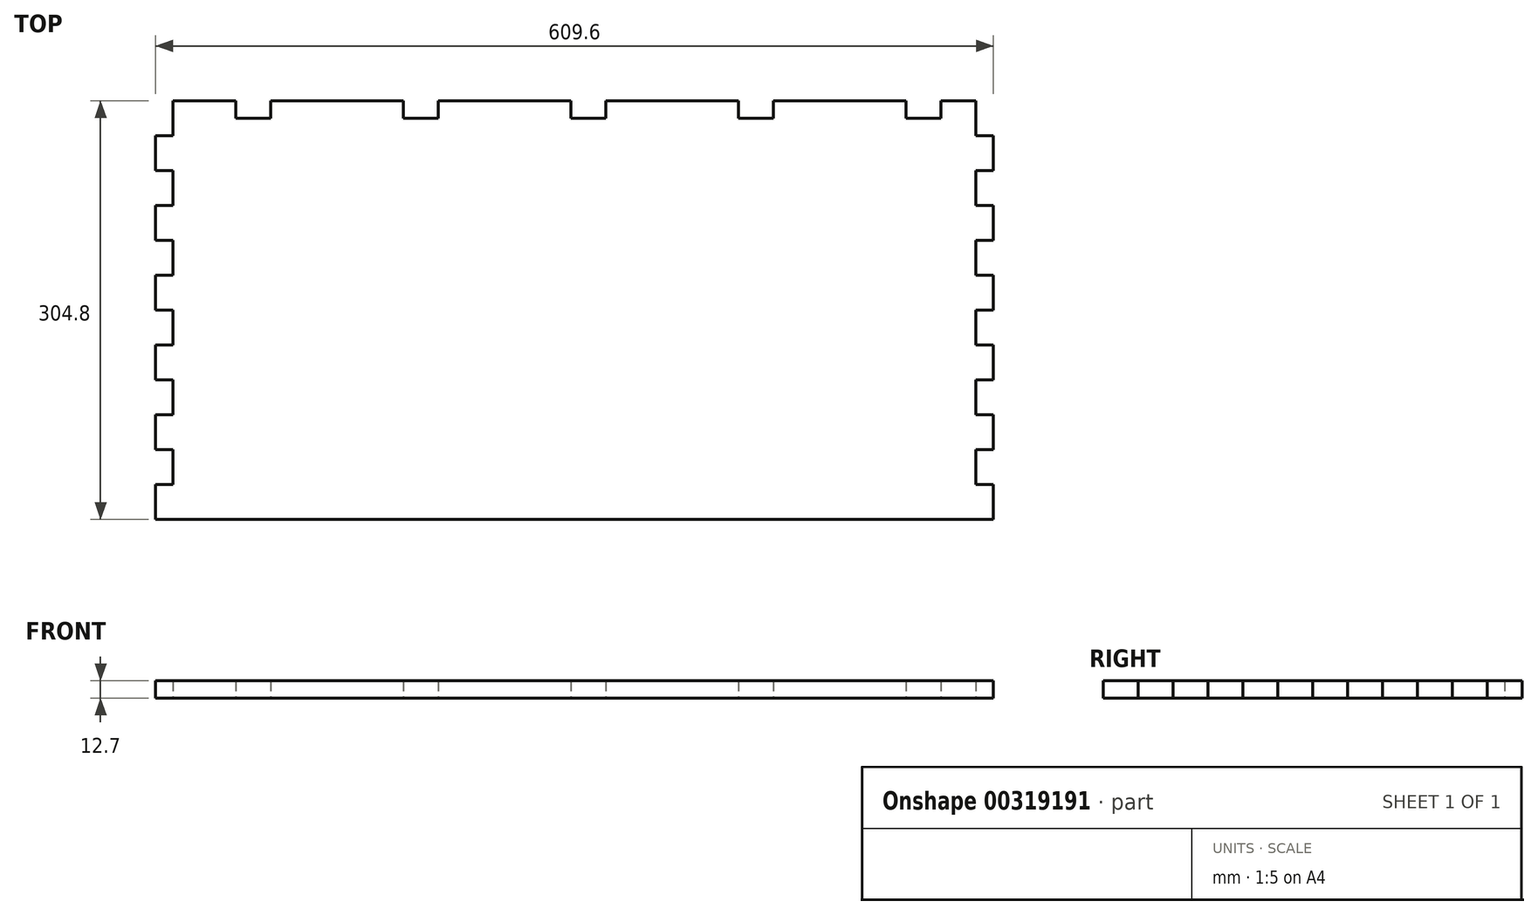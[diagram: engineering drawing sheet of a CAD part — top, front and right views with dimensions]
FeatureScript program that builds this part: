
annotation { "Feature Type Name" : "Feature", "Feature Type Description" : "" }
export const myFeature = defineFeature(function(context is Context, id is Id, definition is map)
    precondition{}
    {
        {
            var Q0;
            Q0=qCreatedBy(makeId("Top.planeOp"),FACE);
            var sketch = newSketch(context, id + "F0", { "sketchPlane" : qUnion([Q0])});
            skLineSegment(sketch, "E0.bottom", {"start": v(-304.8, 152.4) * mm, "end": v(304.8, 152.4) * mm});
            skLineSegment(sketch, "E0.top", {"start": v(-304.8, -152.4) * mm, "end": v(304.8, -152.4) * mm});
            skLineSegment(sketch, "E0.left", {"start": v(-304.8, 152.4) * mm, "end": v(-304.8, -152.4) * mm});
            skLineSegment(sketch, "E0.right", {"start": v(304.8, 152.4) * mm, "end": v(304.8, -152.4) * mm});
            skPoint(sketch, "E0.middle", {"position": v(0, 0) * mm});
            skLineSegment(sketch, "E1.bottom", {"start": v(-304.8, 152.4) * mm, "end": v(-292.1, 152.4) * mm});
            skLineSegment(sketch, "E1.top", {"start": v(-304.8, 127) * mm, "end": v(-292.1, 127) * mm});
            skLineSegment(sketch, "E1.left", {"start": v(-304.8, 152.4) * mm, "end": v(-304.8, 127) * mm});
            skLineSegment(sketch, "E1.right", {"start": v(-292.1, 152.4) * mm, "end": v(-292.1, 127) * mm});
            skLineSegment(sketch, "E2.0.1.0", {"start": v(-304.8, 76.2) * mm, "end": v(-292.1, 76.2) * mm});
            skLineSegment(sketch, "E2.0.1.1", {"start": v(-304.8, 101.6) * mm, "end": v(-292.1, 101.6) * mm});
            skLineSegment(sketch, "E2.0.1.2", {"start": v(-292.1, 101.6) * mm, "end": v(-292.1, 76.2) * mm});
            skLineSegment(sketch, "E2.0.1.3", {"start": v(-304.8, 101.6) * mm, "end": v(-304.8, 76.2) * mm});
            skLineSegment(sketch, "E2.0.2.0", {"start": v(-304.8, 25.4) * mm, "end": v(-292.1, 25.4) * mm});
            skLineSegment(sketch, "E2.0.2.1", {"start": v(-304.8, 50.8) * mm, "end": v(-292.1, 50.8) * mm});
            skLineSegment(sketch, "E2.0.2.2", {"start": v(-292.1, 50.8) * mm, "end": v(-292.1, 25.4) * mm});
            skLineSegment(sketch, "E2.0.2.3", {"start": v(-304.8, 50.8) * mm, "end": v(-304.8, 25.4) * mm});
            skLineSegment(sketch, "E2.0.3.0", {"start": v(-304.8, -25.4) * mm, "end": v(-292.1, -25.4) * mm});
            skLineSegment(sketch, "E2.0.3.1", {"start": v(-304.8, 0) * mm, "end": v(-292.1, 0) * mm});
            skLineSegment(sketch, "E2.0.3.2", {"start": v(-292.1, 0) * mm, "end": v(-292.1, -25.4) * mm});
            skLineSegment(sketch, "E2.0.3.3", {"start": v(-304.8, 0) * mm, "end": v(-304.8, -25.4) * mm});
            skLineSegment(sketch, "E2.0.4.0", {"start": v(-304.8, -76.2) * mm, "end": v(-292.1, -76.2) * mm});
            skLineSegment(sketch, "E2.0.4.1", {"start": v(-304.8, -50.8) * mm, "end": v(-292.1, -50.8) * mm});
            skLineSegment(sketch, "E2.0.4.2", {"start": v(-292.1, -50.8) * mm, "end": v(-292.1, -76.2) * mm});
            skLineSegment(sketch, "E2.0.4.3", {"start": v(-304.8, -50.8) * mm, "end": v(-304.8, -76.2) * mm});
            skLineSegment(sketch, "E2.0.5.0", {"start": v(-304.8, -127) * mm, "end": v(-292.1, -127) * mm});
            skLineSegment(sketch, "E2.0.5.1", {"start": v(-304.8, -101.6) * mm, "end": v(-292.1, -101.6) * mm});
            skLineSegment(sketch, "E2.0.5.2", {"start": v(-292.1, -101.6) * mm, "end": v(-292.1, -127) * mm});
            skLineSegment(sketch, "E2.0.5.3", {"start": v(-304.8, -101.6) * mm, "end": v(-304.8, -127) * mm});
            skLineSegment(sketch, "E2.direction1", {"start": v(-304.8, 127) * mm, "end": v(-279.4, 127) * mm, "construction": true});
            skLineSegment(sketch, "E2.direction2", {"start": v(-304.8, 127) * mm, "end": v(-304.8, 76.2) * mm, "construction": true});
            skLineSegment(sketch, "E3.bottom", {"start": v(304.8, 152.4) * mm, "end": v(292.1, 152.4) * mm});
            skLineSegment(sketch, "E3.top", {"start": v(304.8, 127) * mm, "end": v(292.1, 127) * mm});
            skLineSegment(sketch, "E3.left", {"start": v(304.8, 152.4) * mm, "end": v(304.8, 127) * mm});
            skLineSegment(sketch, "E3.right", {"start": v(292.1, 152.4) * mm, "end": v(292.1, 127) * mm});
            skLineSegment(sketch, "E4.0.1.0", {"start": v(304.8, 76.2) * mm, "end": v(292.1, 76.2) * mm});
            skLineSegment(sketch, "E4.0.1.1", {"start": v(304.8, 101.6) * mm, "end": v(304.8, 76.2) * mm});
            skLineSegment(sketch, "E4.0.1.2", {"start": v(304.8, 101.6) * mm, "end": v(292.1, 101.6) * mm});
            skLineSegment(sketch, "E4.0.1.3", {"start": v(292.1, 101.6) * mm, "end": v(292.1, 76.2) * mm});
            skLineSegment(sketch, "E4.0.2.0", {"start": v(304.8, 25.4) * mm, "end": v(292.1, 25.4) * mm});
            skLineSegment(sketch, "E4.0.2.1", {"start": v(304.8, 50.8) * mm, "end": v(304.8, 25.4) * mm});
            skLineSegment(sketch, "E4.0.2.2", {"start": v(304.8, 50.8) * mm, "end": v(292.1, 50.8) * mm});
            skLineSegment(sketch, "E4.0.2.3", {"start": v(292.1, 50.8) * mm, "end": v(292.1, 25.4) * mm});
            skLineSegment(sketch, "E4.0.3.0", {"start": v(304.8, -25.4) * mm, "end": v(292.1, -25.4) * mm});
            skLineSegment(sketch, "E4.0.3.1", {"start": v(304.8, 0) * mm, "end": v(304.8, -25.4) * mm});
            skLineSegment(sketch, "E4.0.3.2", {"start": v(304.8, 0) * mm, "end": v(292.1, 0) * mm});
            skLineSegment(sketch, "E4.0.3.3", {"start": v(292.1, 0) * mm, "end": v(292.1, -25.4) * mm});
            skLineSegment(sketch, "E4.0.4.0", {"start": v(304.8, -76.2) * mm, "end": v(292.1, -76.2) * mm});
            skLineSegment(sketch, "E4.0.4.1", {"start": v(304.8, -50.8) * mm, "end": v(304.8, -76.2) * mm});
            skLineSegment(sketch, "E4.0.4.2", {"start": v(304.8, -50.8) * mm, "end": v(292.1, -50.8) * mm});
            skLineSegment(sketch, "E4.0.4.3", {"start": v(292.1, -50.8) * mm, "end": v(292.1, -76.2) * mm});
            skLineSegment(sketch, "E4.0.5.0", {"start": v(304.8, -127) * mm, "end": v(292.1, -127) * mm});
            skLineSegment(sketch, "E4.0.5.1", {"start": v(304.8, -101.6) * mm, "end": v(304.8, -127) * mm});
            skLineSegment(sketch, "E4.0.5.2", {"start": v(304.8, -101.6) * mm, "end": v(292.1, -101.6) * mm});
            skLineSegment(sketch, "E4.0.5.3", {"start": v(292.1, -101.6) * mm, "end": v(292.1, -127) * mm});
            skLineSegment(sketch, "E4.direction1", {"start": v(292.1, 127) * mm, "end": v(317.5, 127) * mm, "construction": true});
            skLineSegment(sketch, "E4.direction2", {"start": v(292.1, 127) * mm, "end": v(292.1, 76.2) * mm, "construction": true});
            skLineSegment(sketch, "E5.bottom", {"start": v(266.7, 152.4) * mm, "end": v(241.3, 152.4) * mm});
            skLineSegment(sketch, "E5.top", {"start": v(266.7, 139.7) * mm, "end": v(241.3, 139.7) * mm});
            skLineSegment(sketch, "E5.left", {"start": v(266.7, 152.4) * mm, "end": v(266.7, 139.7) * mm});
            skLineSegment(sketch, "E5.right", {"start": v(241.3, 152.4) * mm, "end": v(241.3, 139.7) * mm});
            skLineSegment(sketch, "E6.1.0.0", {"start": v(119.38, 152.4) * mm, "end": v(119.38, 139.7) * mm});
            skLineSegment(sketch, "E6.1.0.1", {"start": v(144.78, 139.7) * mm, "end": v(119.38, 139.7) * mm});
            skLineSegment(sketch, "E6.1.0.2", {"start": v(144.78, 152.4) * mm, "end": v(144.78, 139.7) * mm});
            skLineSegment(sketch, "E6.1.0.3", {"start": v(144.78, 152.4) * mm, "end": v(119.38, 152.4) * mm});
            skLineSegment(sketch, "E6.2.0.0", {"start": v(-2.54, 152.4) * mm, "end": v(-2.54, 139.7) * mm});
            skLineSegment(sketch, "E6.2.0.1", {"start": v(22.86, 139.7) * mm, "end": v(-2.54, 139.7) * mm});
            skLineSegment(sketch, "E6.2.0.2", {"start": v(22.86, 152.4) * mm, "end": v(22.86, 139.7) * mm});
            skLineSegment(sketch, "E6.2.0.3", {"start": v(22.86, 152.4) * mm, "end": v(-2.54, 152.4) * mm});
            skLineSegment(sketch, "E6.3.0.0", {"start": v(-124.46, 152.4) * mm, "end": v(-124.46, 139.7) * mm});
            skLineSegment(sketch, "E6.3.0.1", {"start": v(-99.06, 139.7) * mm, "end": v(-124.46, 139.7) * mm});
            skLineSegment(sketch, "E6.3.0.2", {"start": v(-99.06, 152.4) * mm, "end": v(-99.06, 139.7) * mm});
            skLineSegment(sketch, "E6.3.0.3", {"start": v(-99.06, 152.4) * mm, "end": v(-124.46, 152.4) * mm});
            skLineSegment(sketch, "E6.4.0.0", {"start": v(-246.38, 152.4) * mm, "end": v(-246.38, 139.7) * mm});
            skLineSegment(sketch, "E6.4.0.1", {"start": v(-220.98, 139.7) * mm, "end": v(-246.38, 139.7) * mm});
            skLineSegment(sketch, "E6.4.0.2", {"start": v(-220.98, 152.4) * mm, "end": v(-220.98, 139.7) * mm});
            skLineSegment(sketch, "E6.4.0.3", {"start": v(-220.98, 152.4) * mm, "end": v(-246.38, 152.4) * mm});
            skLineSegment(sketch, "E6.direction1", {"start": v(241.3, 139.7) * mm, "end": v(119.38, 139.7) * mm, "construction": true});
            skSolve(sketch);
        }
        {
            var Q0;
            {var subQ13=sQuery(id+"F0.wireOp",EDGE,"E0.top");Q0=makeQuery(id+"F0.imprint","IMPRINT",FACE,{"disambiguationData":[TD([[makeQuery(id+"F0.imprint","IMPRINT",EDGE,{"derivedFrom":subQ13}),1.0]])]});}
            extrude(context, id + "F1", {"entities" : qUnion([Q0]), "depth" : 12.7 * mm});
        }
    });
